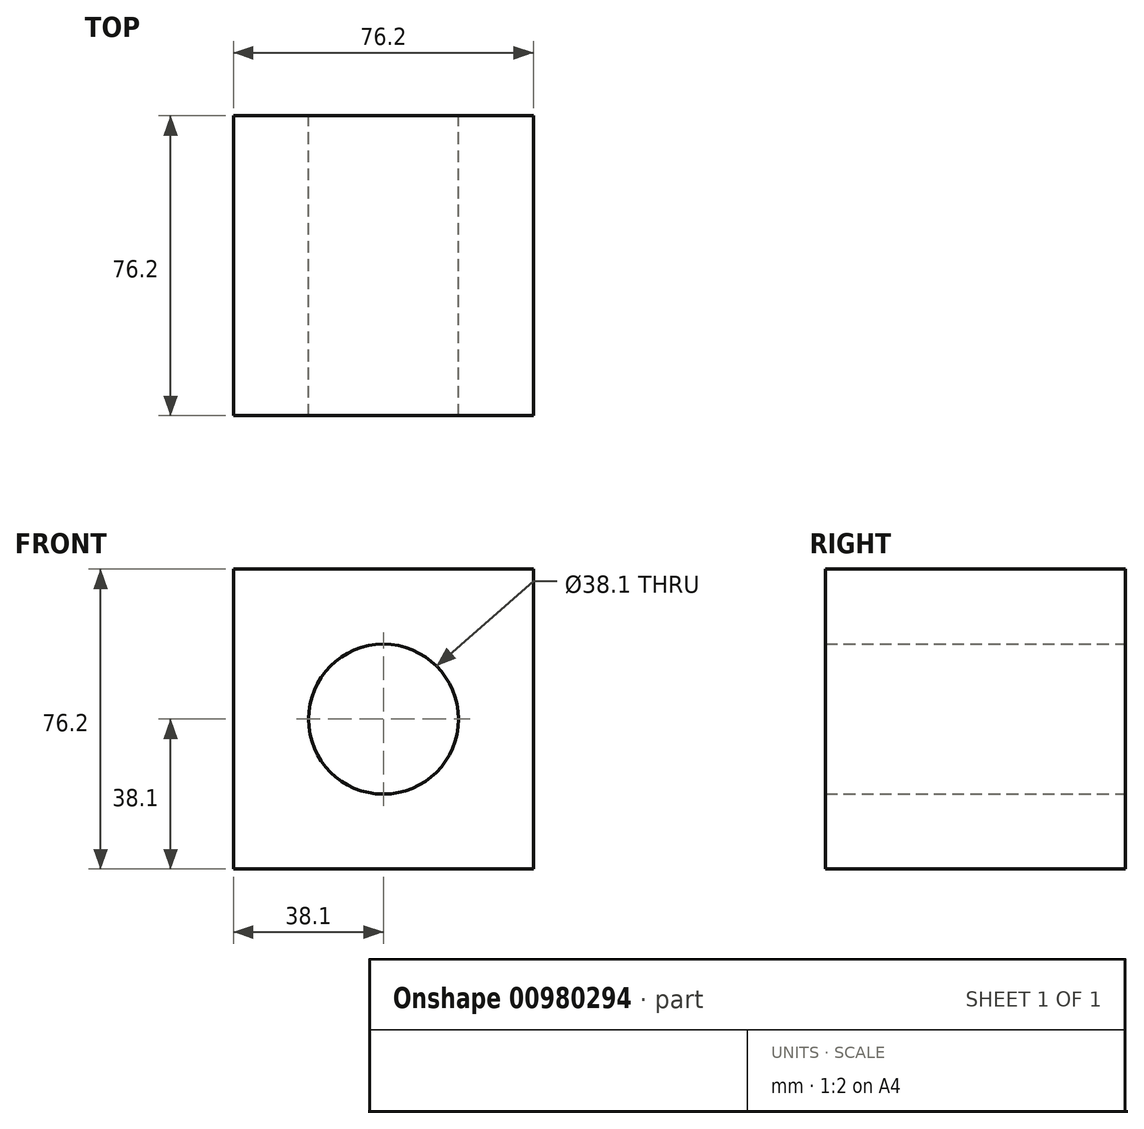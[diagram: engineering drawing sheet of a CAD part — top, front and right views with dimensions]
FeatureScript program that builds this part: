
annotation { "Feature Type Name" : "Feature", "Feature Type Description" : "" }
export const myFeature = defineFeature(function(context is Context, id is Id, definition is map)
    precondition{}
    {
        {
            var Q0;
            Q0=qCreatedBy(makeId("Front.planeOp"),FACE);
            var sketch = newSketch(context, id + "F0", { "sketchPlane" : qUnion([Q0])});
            skLineSegment(sketch, "E0.bottom", {"start": v(0, 0) * mm, "end": v(76.2, 0) * mm});
            skLineSegment(sketch, "E0.top", {"start": v(0, 76.2) * mm, "end": v(76.2, 76.2) * mm});
            skLineSegment(sketch, "E0.left", {"start": v(0, 0) * mm, "end": v(0, 76.2) * mm});
            skLineSegment(sketch, "E0.right", {"start": v(76.2, 0) * mm, "end": v(76.2, 76.2) * mm});
            skCircle(sketch, "E1", {"center": v(38.1, 38.1) * mm, "radius": 19.05 * mm});
            skPoint(sketch, "E1.centerSnap0", {"position": v(76.2, 38.1) * mm});
            skPoint(sketch, "E1.centerSnap1", {"position": v(38.1, 76.2) * mm});
            skSolve(sketch);
        }
        {
            var Q0;
            Q0=makeQuery(id+"F0.imprint","IMPRINT",FACE,{"disambiguationData":[TD([[makeQuery(id+"F0.imprint","IMPRINT",EDGE,{"derivedFrom":sQuery(id+"F0.wireOp",EDGE,"E0.bottom")}),1.0]])]});
            extrude(context, id + "F1", {"entities" : qUnion([Q0]), "depth" : 76.2 * mm, "offsetDistance" : 25.4 * mm});
        }
    });
